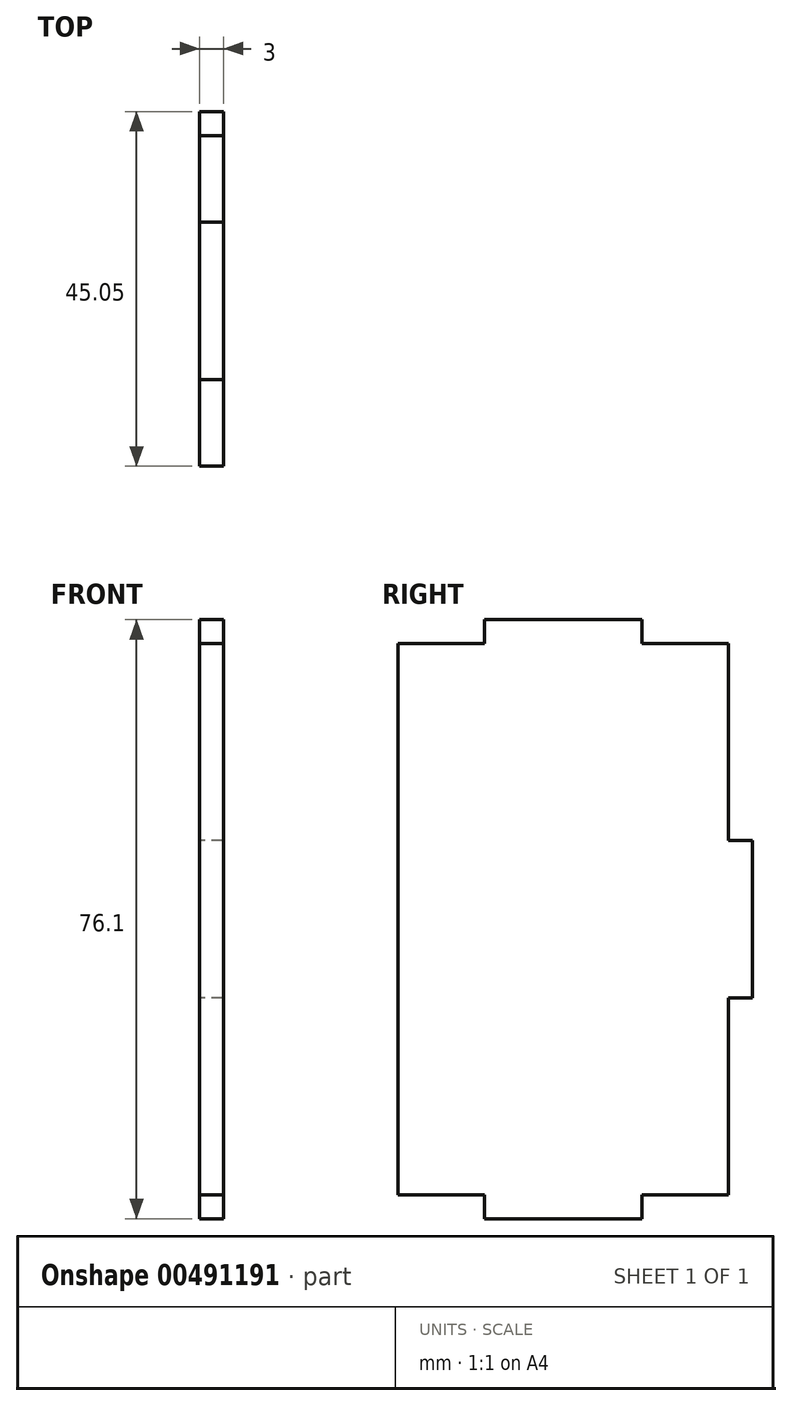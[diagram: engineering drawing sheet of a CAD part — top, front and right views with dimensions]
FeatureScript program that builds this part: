
annotation { "Feature Type Name" : "Feature", "Feature Type Description" : "" }
export const myFeature = defineFeature(function(context is Context, id is Id, definition is map)
    precondition{}
    {
        {
            var Q0;
            Q0=qCreatedBy(makeId("Right.planeOp"),FACE);
            var sketch = newSketch(context, id + "F0", { "sketchPlane" : qUnion([Q0])});
            skLineSegment(sketch, "E0.bottom", {"start": v(21, -35) * mm, "end": v(-21, -35) * mm});
            skLineSegment(sketch, "E0.top", {"start": v(21, 35) * mm, "end": v(-21, 35) * mm});
            skLineSegment(sketch, "E0.left", {"start": v(21, -35) * mm, "end": v(21, 35) * mm});
            skLineSegment(sketch, "E0.right", {"start": v(-21, -35) * mm, "end": v(-21, 35) * mm});
            skPoint(sketch, "E0.middle", {"position": v(0, 0) * mm});
            skLineSegment(sketch, "E1.bottom", {"start": v(24.05, -10) * mm, "end": v(21, -10) * mm});
            skLineSegment(sketch, "E1.top", {"start": v(24.05, 10) * mm, "end": v(21, 10) * mm});
            skLineSegment(sketch, "E1.left", {"start": v(24.05, -10) * mm, "end": v(24.05, 10) * mm});
            skLineSegment(sketch, "E1.right", {"start": v(21, -10) * mm, "end": v(21, 10) * mm});
            skPoint(sketch, "E1.middle", {"position": v(22.53, 0) * mm});
            skLineSegment(sketch, "E2.bottom", {"start": v(10, 35) * mm, "end": v(-10, 35) * mm});
            skLineSegment(sketch, "E2.top", {"start": v(10, 38.05) * mm, "end": v(-10, 38.05) * mm});
            skLineSegment(sketch, "E2.left", {"start": v(10, 35) * mm, "end": v(10, 38.05) * mm});
            skLineSegment(sketch, "E2.right", {"start": v(-10, 35) * mm, "end": v(-10, 38.05) * mm});
            skPoint(sketch, "E2.middle", {"position": v(0, 36.52) * mm});
            skLineSegment(sketch, "E3.bottom", {"start": v(10, -38.05) * mm, "end": v(-10, -38.05) * mm});
            skLineSegment(sketch, "E3.top", {"start": v(10, -35) * mm, "end": v(-10, -35) * mm});
            skLineSegment(sketch, "E3.left", {"start": v(10, -38.05) * mm, "end": v(10, -35) * mm});
            skLineSegment(sketch, "E3.right", {"start": v(-10, -38.05) * mm, "end": v(-10, -35) * mm});
            skPoint(sketch, "E3.middle", {"position": v(0, -36.52) * mm});
            skSolve(sketch);
        }
        {
            var Q0;
            Q0 = qSketchRegion(id + "F0", true);
            extrude(context, id + "F1", {"entities" : qUnion([Q0]), "depth" : 3 * mm});
        }
    });
